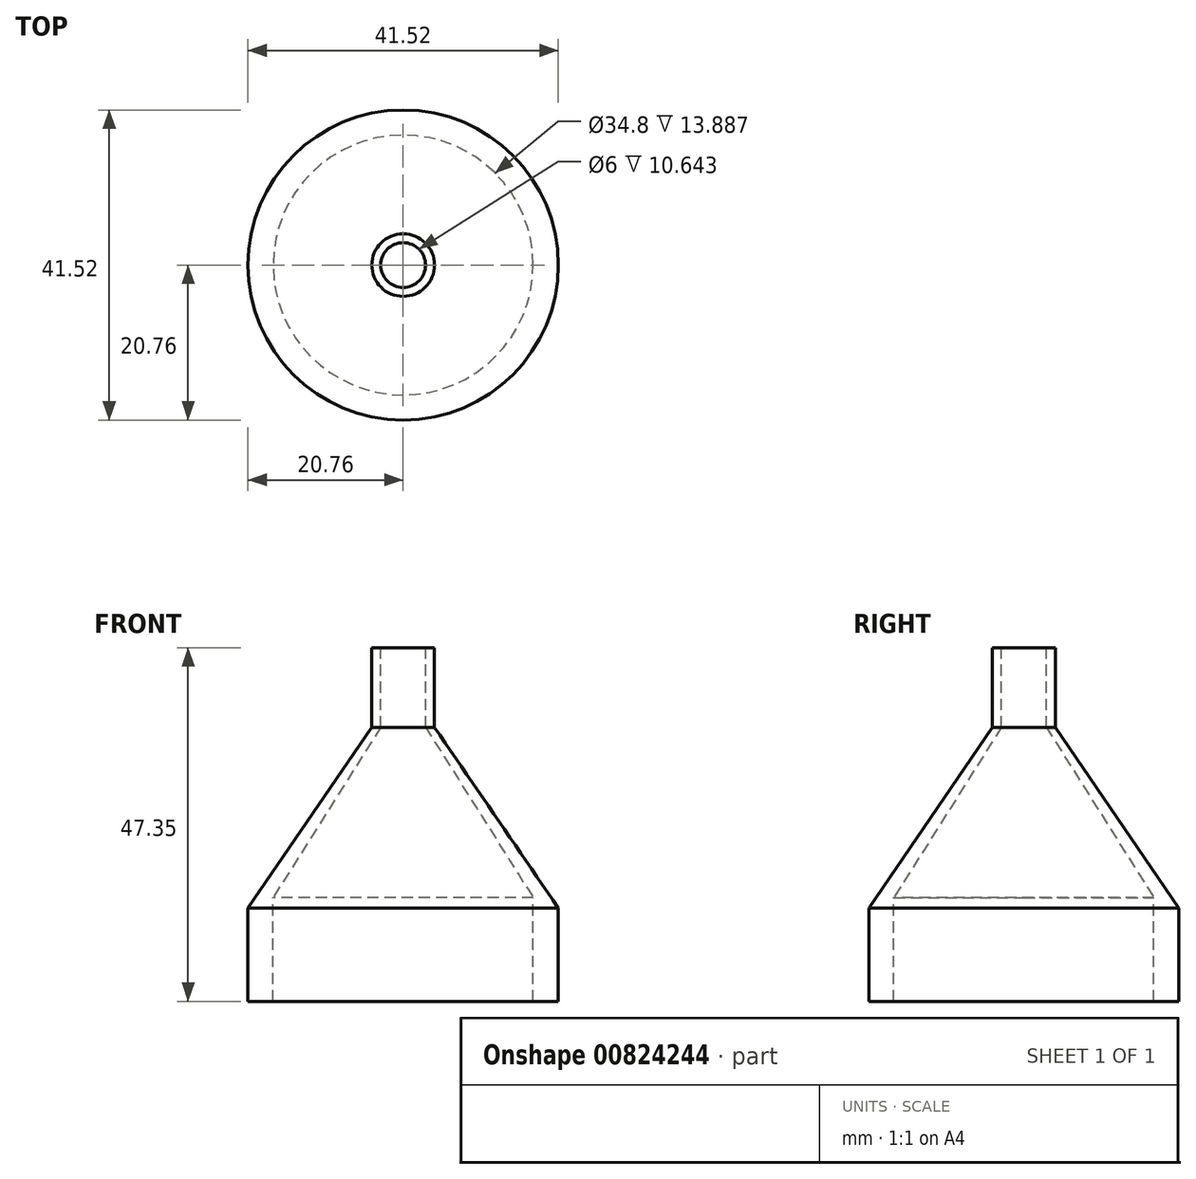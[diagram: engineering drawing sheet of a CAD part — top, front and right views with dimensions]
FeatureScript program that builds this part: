
annotation { "Feature Type Name" : "Feature", "Feature Type Description" : "" }
export const myFeature = defineFeature(function(context is Context, id is Id, definition is map)
    precondition{}
    {
        {
            var Q0;
            Q0=qCreatedBy(makeId("Front.planeOp"),FACE);
            var sketch = newSketch(context, id + "F0", { "sketchPlane" : qUnion([Q0])});
            skLineSegment(sketch, "E0", {"start": v(-20.76, 0) * mm, "end": v(-20.76, 12.49) * mm});
            skLineSegment(sketch, "E1", {"start": v(-17.4, 13.89) * mm, "end": v(-17.4, 0) * mm});
            skLineSegment(sketch, "E2", {"start": v(-20.76, 0) * mm, "end": v(-17.4, 0) * mm});
            skLineSegment(sketch, "E3", {"start": v(0, 49.71) * mm, "end": v(0, 0) * mm});
            skLineSegment(sketch, "E4", {"start": v(-3, 47.35) * mm, "end": v(-3, 36.7) * mm});
            skLineSegment(sketch, "E5", {"start": v(-3, 36.7) * mm, "end": v(-17.4, 13.89) * mm});
            skLineSegment(sketch, "E6", {"start": v(-4.2, 36.7) * mm, "end": v(-20.76, 12.49) * mm});
            skLineSegment(sketch, "E7", {"start": v(-4.2, 36.7) * mm, "end": v(-4.2, 47.35) * mm});
            skLineSegment(sketch, "E8", {"start": v(-3, 47.35) * mm, "end": v(-4.2, 47.35) * mm});
            skSolve(sketch);
        }
        {
            var Q0;
            Q0=makeQuery(id+"F0.imprint","IMPRINT",FACE,{"disambiguationData":[TD([[makeQuery(id+"F0.imprint","IMPRINT",EDGE,{"derivedFrom":sQuery(id+"F0.wireOp",EDGE,"E0")}),-1.0]])]});
            var Q1;
            Q1=sQuery(id+"F0.wireOp",EDGE,"E3");
            revolve(context, id + "F1", {"surfaceOperationType" : NewSurfaceOperationType.NEW, "entities" : qUnion([Q0]), "axis" : qUnion([Q1]), "revolveType" : RevolveType.FULL});
        }
    });
